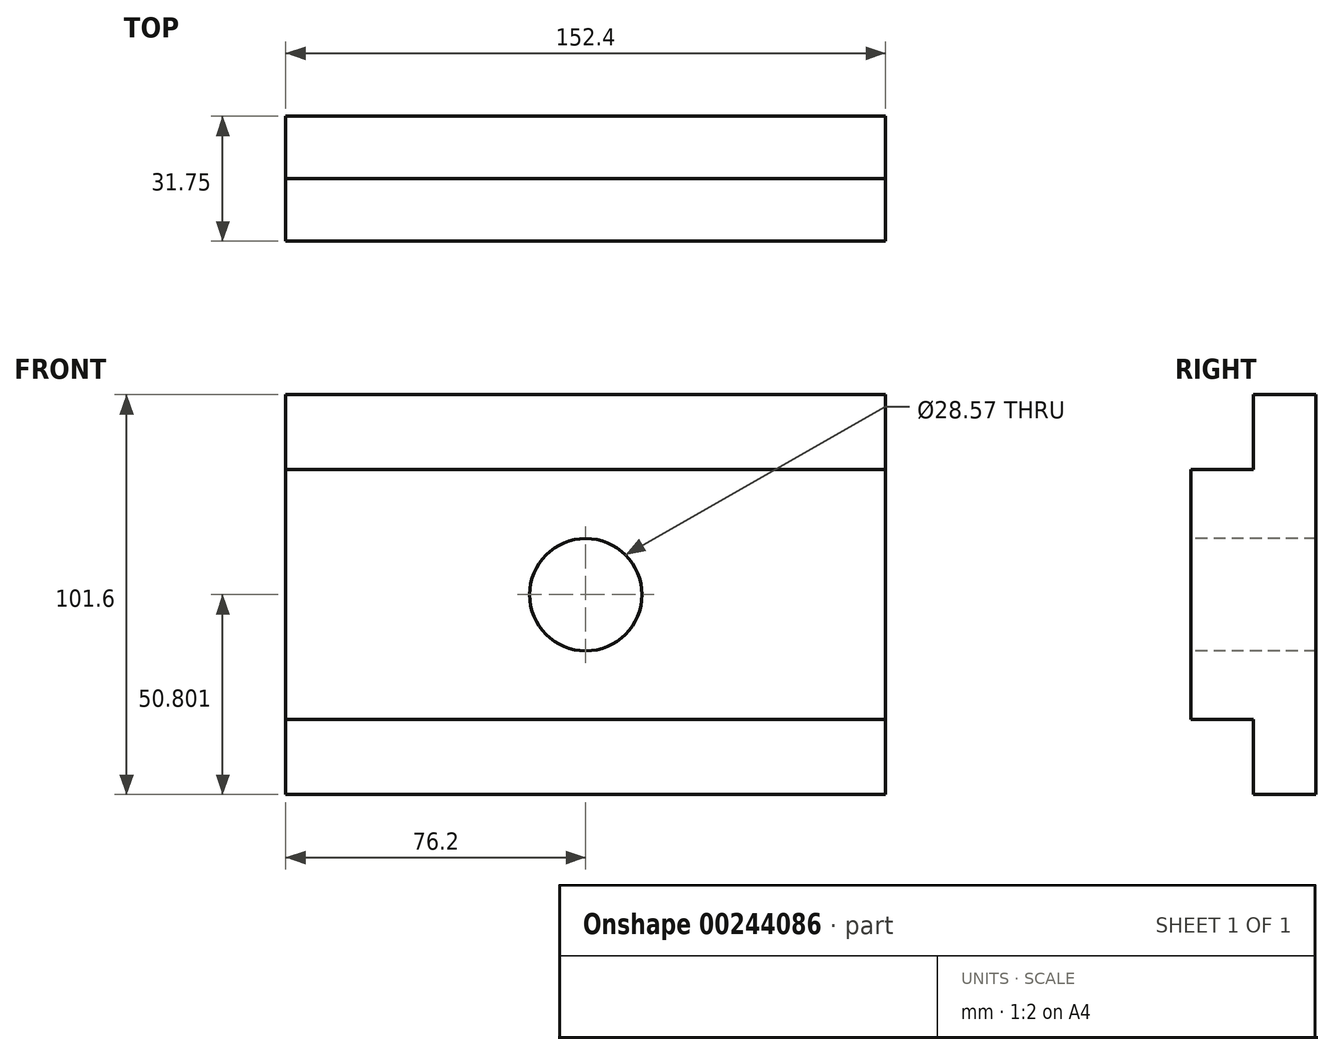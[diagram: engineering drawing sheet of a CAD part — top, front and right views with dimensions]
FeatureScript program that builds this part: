
annotation { "Feature Type Name" : "Feature", "Feature Type Description" : "" }
export const myFeature = defineFeature(function(context is Context, id is Id, definition is map)
    precondition{}
    {
        {
            var Q0;
            Q0=qCreatedBy(makeId("Right.planeOp"),FACE);
            var sketch = newSketch(context, id + "F0", { "sketchPlane" : qUnion([Q0])});
            skLineSegment(sketch, "E0.bottom", {"start": v(35.8, 74.06) * mm, "end": v(19.92, 74.06) * mm});
            skLineSegment(sketch, "E0.top", {"start": v(35.8, -27.54) * mm, "end": v(19.92, -27.54) * mm});
            skLineSegment(sketch, "E0.left", {"start": v(35.8, 74.06) * mm, "end": v(35.8, -27.54) * mm});
            skLineSegment(sketch, "E0.right", {"start": v(19.92, 74.06) * mm, "end": v(19.92, 55.01) * mm});
            skLineSegment(sketch, "E1.bottom", {"start": v(19.92, 55.01) * mm, "end": v(4.04, 55.01) * mm});
            skLineSegment(sketch, "E1.top", {"start": v(19.92, -8.49) * mm, "end": v(4.04, -8.49) * mm});
            skLineSegment(sketch, "E1.right", {"start": v(4.04, 55.01) * mm, "end": v(4.04, -8.49) * mm});
            skLineSegment(sketch, "E2.trimOffspring", {"start": v(19.92, -8.49) * mm, "end": v(19.92, -27.54) * mm});
            skSolve(sketch);
        }
        {
            var Q0;
            Q0 = qSketchRegion(id + "F0", true);
            extrude(context, id + "F1", {"entities" : qUnion([Q0]), "depth" : 152.4 * mm});
        }
        {
            var Q0;
            Q0=qCreatedBy(makeId("Front.planeOp"),FACE);
            var sketch = newSketch(context, id + "F2", { "sketchPlane" : qUnion([Q0])});
            skCircle(sketch, "E3", {"center": v(76.2, 23.26) * mm, "radius": 14.29 * mm});
            skSolve(sketch);
        }
        {
            var Q0;
            Q0=makeQuery(id+"F2.imprint","IMPRINT",FACE,{"disambiguationData":[TD([[makeQuery(id+"F2.imprint","IMPRINT",EDGE,{"derivedFrom":sQuery(id+"F2.wireOp",EDGE,"E3")}),1.0]])]});
            extrude(context, id + "F3", {"entities" : qUnion([Q0]), "operationType" : NewBodyOperationType.REMOVE, "endBound" : BoundingType.THROUGH_ALL, "oppositeDirection" : true, "depth" : 25.4 * mm});
        }
    });
